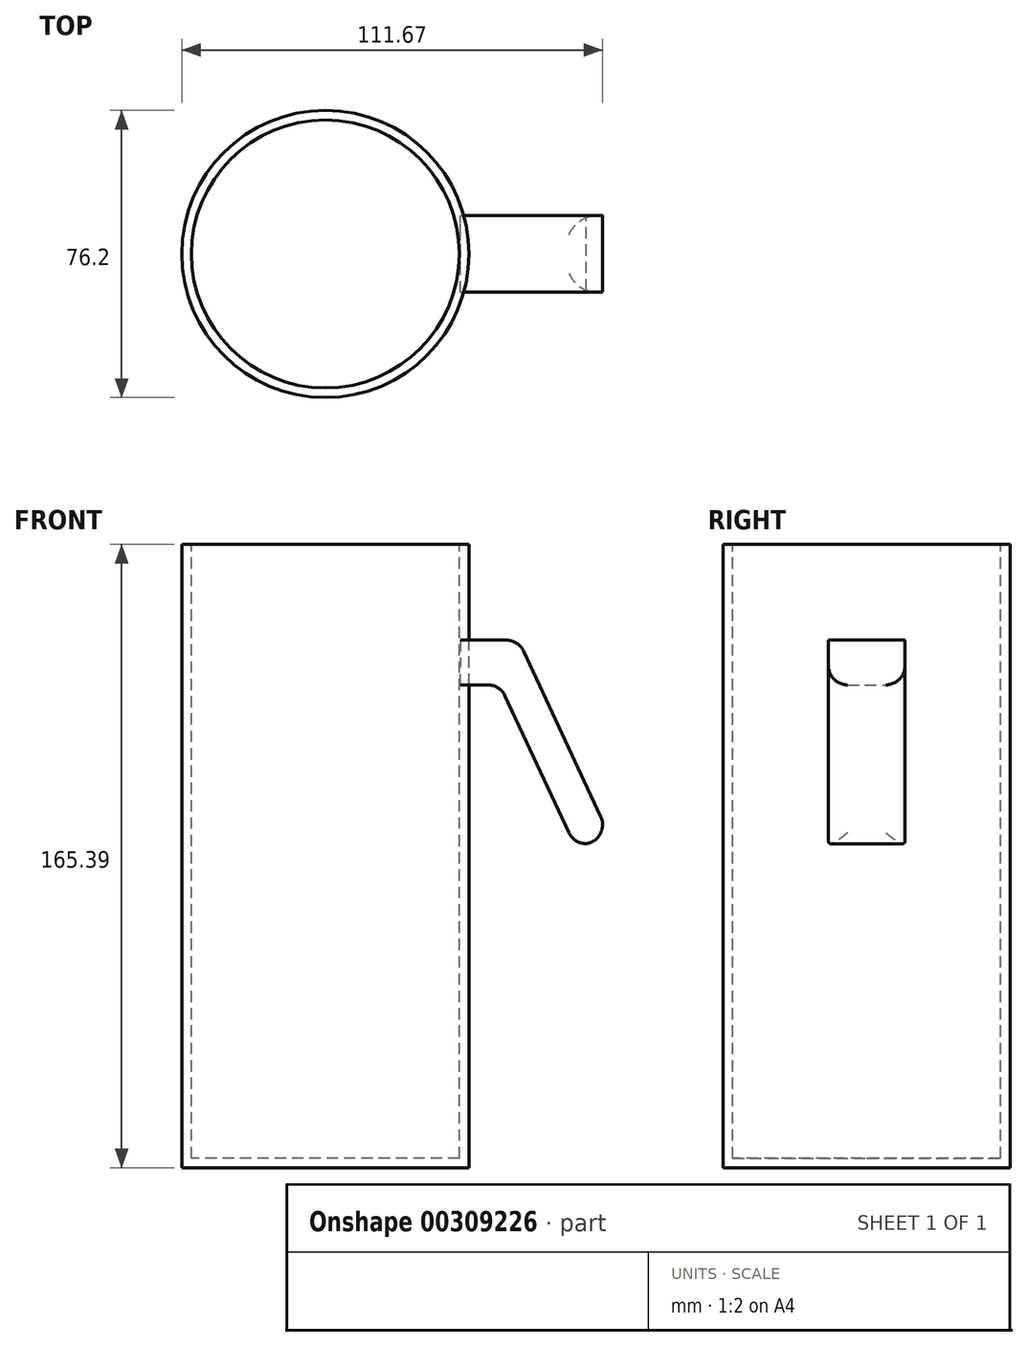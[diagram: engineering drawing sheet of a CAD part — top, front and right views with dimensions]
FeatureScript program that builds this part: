
annotation { "Feature Type Name" : "Feature", "Feature Type Description" : "" }
export const myFeature = defineFeature(function(context is Context, id is Id, definition is map)
    precondition{}
    {
        {
            var Q0;
            Q0=qCreatedBy(makeId("Front.planeOp"),FACE);
            var sketch = newSketch(context, id + "F0", { "sketchPlane" : qUnion([Q0])});
            skLineSegment(sketch, "E0", {"start": v(-18.24, 79.4) * mm, "end": v(19.86, 79.4) * mm});
            skLineSegment(sketch, "E1", {"start": v(-18.24, 79.4) * mm, "end": v(-18.24, -85.98) * mm});
            skLineSegment(sketch, "E2", {"start": v(-18.24, -85.98) * mm, "end": v(19.86, -85.98) * mm});
            skLineSegment(sketch, "E3", {"start": v(17.56, 54) * mm, "end": v(33.01, 54) * mm});
            skLineSegment(sketch, "E4", {"start": v(33.01, 54) * mm, "end": v(58.2, 0) * mm});
            skLineSegment(sketch, "E5", {"start": v(47.74, 0) * mm, "end": v(58.2, 0) * mm});
            skLineSegment(sketch, "E6", {"start": v(17.56, 42.08) * mm, "end": v(28.08, 42.17) * mm});
            skLineSegment(sketch, "E7", {"start": v(47.74, 0) * mm, "end": v(28.08, 42.17) * mm});
            skLineSegment(sketch, "E8", {"start": v(19.86, 79.4) * mm, "end": v(19.86, -85.98) * mm});
            skLineSegment(sketch, "E9", {"start": v(17.56, 54) * mm, "end": v(17.56, 42.08) * mm});
            skSolve(sketch);
        }
        {
            var Q0;
            {var subQ7=sQuery(id+"F0.wireOp",EDGE,"E0");Q0=makeQuery(id+"F0.imprint","IMPRINT",FACE,{"disambiguationData":[TD([[makeQuery(id+"F0.imprint","IMPRINT",EDGE,{"derivedFrom":subQ7}),-1.0]])]});}
            var Q1;
            {var subQ0=sQuery(id+"F0.wireOp",EDGE,"E9");Q1=makeQuery(id+"F0.imprint","IMPRINT",FACE,{"disambiguationData":[TD([[makeQuery(id+"F0.imprint","IMPRINT",EDGE,{"derivedFrom":subQ0}),1.0]])]});}
            var Q2;
            Q2=sQuery(id+"F0.wireOp",EDGE,"E1");
            revolve(context, id + "F1", {"entities" : qUnion([Q0, Q1]), "axis" : qUnion([Q2]), "revolveType" : RevolveType.FULL});
        }
        {
            var Q0;
            {var subQ4=sQuery(id+"F0.wireOp",EDGE,"E4");Q0=makeQuery(id+"F0.imprint","IMPRINT",FACE,{"disambiguationData":[TD([[makeQuery(id+"F0.imprint","IMPRINT",EDGE,{"derivedFrom":subQ4}),-1.0]])]});}
            var Q1;
            {var subQ0=sQuery(id+"F0.wireOp",EDGE,"E9");Q1=makeQuery(id+"F0.imprint","IMPRINT",FACE,{"disambiguationData":[TD([[makeQuery(id+"F0.imprint","IMPRINT",EDGE,{"derivedFrom":subQ0}),1.0]])]});}
            extrude(context, id + "F2", {"entities" : qUnion([Q0, Q1]), "endBound" : BoundingType.SYMMETRIC, "depth" : 20.32 * mm});
        }
        {
            var Q0;
            Q0=makeQuery(id+"F2.opExtrude","SWEPT_EDGE",EDGE,{"disambiguationData":[OSD([sQuery(id+"F0.wireOp",EDGE,"E3"),sQuery(id+"F0.wireOp",EDGE,"E4")])]});
            fillet(context, id + "F3", {"entities" : qUnion([Q0]), "radius" : 5.08 * mm, "tangentPropagation" : true, "allowEdgeOverflow" : false});
        }
        {
            var Q0;
            Q0=makeQuery(id+"F1.opRevolve","SWEPT_FACE",FACE,{"disambiguationData":[OSD([sQuery(id+"F0.wireOp",EDGE,"E0")])]});
            shell(context, id + "F4", {"entities" : qUnion([Q0]), "thickness" : 2.54 * mm});
        }
        {
            var Q0;
            Q0=makeQuery(id+"F2.opExtrude","SWEPT_EDGE",EDGE,{"disambiguationData":[OSD([sQuery(id+"F0.wireOp",EDGE,"E6"),sQuery(id+"F0.wireOp",EDGE,"E7")])]});
            fillet(context, id + "F5", {"entities" : qUnion([Q0]), "radius" : 5.08 * mm, "tangentPropagation" : true, "allowEdgeOverflow" : false});
        }
        {
            var Q0;
            Q0=makeQuery(id+"F2.opExtrude","SWEPT_EDGE",EDGE,{"disambiguationData":[OSD([sQuery(id+"F0.wireOp",EDGE,"E5"),sQuery(id+"F0.wireOp",EDGE,"E7")])]});
            fillet(context, id + "F6", {"entities" : qUnion([Q0]), "radius" : 5.08 * mm, "tangentPropagation" : true, "allowEdgeOverflow" : false});
        }
        {
            var Q0;
            Q0=makeQuery(id+"F2.opExtrude","SWEPT_EDGE",EDGE,{"disambiguationData":[OSD([sQuery(id+"F0.wireOp",EDGE,"E4"),sQuery(id+"F0.wireOp",EDGE,"E5")])]});
            fillet(context, id + "F7", {"entities" : qUnion([Q0]), "radius" : 5.08 * mm, "tangentPropagation" : true, "allowEdgeOverflow" : false});
        }
        {
            var Q0;
            Q0=makeQuery(id+"F2.opExtrude","CAP_EDGE",EDGE,{"disambiguationData":[OSD([sQuery(id+"F0.wireOp",EDGE,"E7")])],"isStart":false});
            fillet(context, id + "F8", {"entities" : qUnion([Q0]), "radius" : 5.08 * mm, "tangentPropagation" : true, "allowEdgeOverflow" : false});
        }
        {
            var Q0;
            Q0=makeQuery(id+"F2.opExtrude","CAP_EDGE",EDGE,{"disambiguationData":[OSD([sQuery(id+"F0.wireOp",EDGE,"E7")])],"isStart":true});
            fillet(context, id + "F9", {"entities" : qUnion([Q0]), "radius" : 5.08 * mm, "tangentPropagation" : true, "allowEdgeOverflow" : false});
        }
    });
